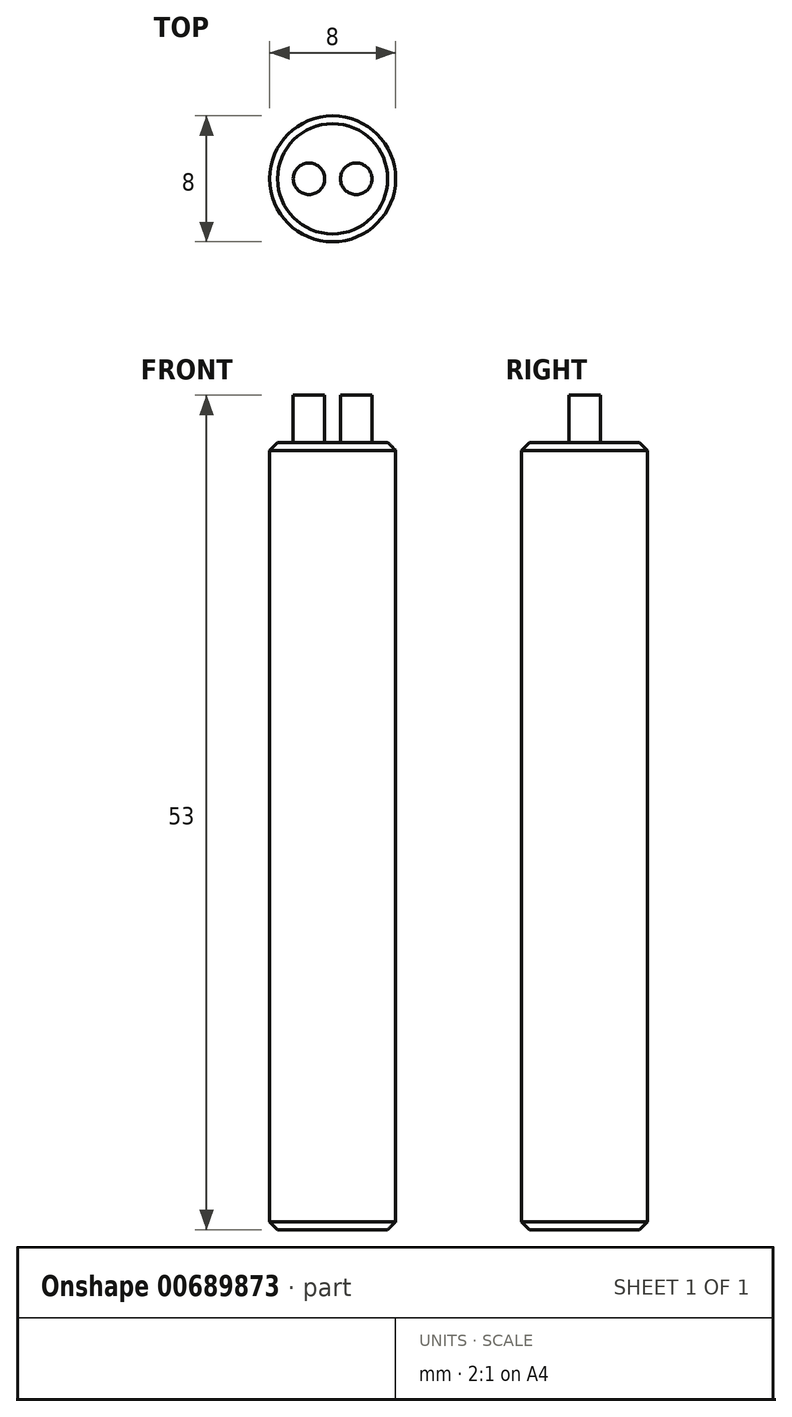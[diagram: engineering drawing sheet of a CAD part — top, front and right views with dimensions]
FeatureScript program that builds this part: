
annotation { "Feature Type Name" : "Feature", "Feature Type Description" : "" }
export const myFeature = defineFeature(function(context is Context, id is Id, definition is map)
    precondition{}
    {
        {
            var Q0;
            Q0=qCreatedBy(makeId("Top.planeOp"),FACE);
            var sketch = newSketch(context, id + "F0", { "sketchPlane" : qUnion([Q0])});
            skCircle(sketch, "E0", {"center": v(0, 0) * mm, "radius": 4 * mm});
            skSolve(sketch);
        }
        {
            var Q0;
            Q0 = qSketchRegion(id + "F0", true);
            extrude(context, id + "F1", {"entities" : qUnion([Q0]), "depth" : 50 * mm, "offsetDistance" : 25 * mm});
        }
        {
            var Q0;
            Q0=makeQuery(id+"F1.opExtrude","CAP_EDGE",EDGE,{"disambiguationData":[OSD([sQuery(id+"F0.wireOp",EDGE,"E0")])],"isStart":false});
            var Q1;
            Q1=makeQuery(id+"F1.opExtrude","CAP_EDGE",EDGE,{"disambiguationData":[OSD([sQuery(id+"F0.wireOp",EDGE,"E0")])],"isStart":true});
            chamfer(context, id + "F2", {"entities" : qUnion([Q0, Q1]), "width" : .5 * mm, "tangentPropagation" : true});
        }
        {
            var Q0;
            Q0=makeQuery(id+"F1.opExtrude","CAP_FACE",FACE,{"disambiguationData":[OSD([sQuery(id+"F0.wireOp",EDGE,"E0")])],"isStart":false});
            var sketch = newSketch(context, id + "F3", { "sketchPlane" : qUnion([Q0])});
            skCircle(sketch, "E1", {"center": v(1.5, 0) * mm, "radius": 1 * mm});
            skCircle(sketch, "E2", {"center": v(-1.5, 0) * mm, "radius": 1 * mm});
            skSolve(sketch);
        }
        {
            var Q0;
            Q0 = qSketchRegion(id + "F3", true);
            extrude(context, id + "F4", {"entities" : qUnion([Q0]), "operationType" : NewBodyOperationType.ADD, "depth" : 3 * mm, "offsetDistance" : 25 * mm});
        }
    });
